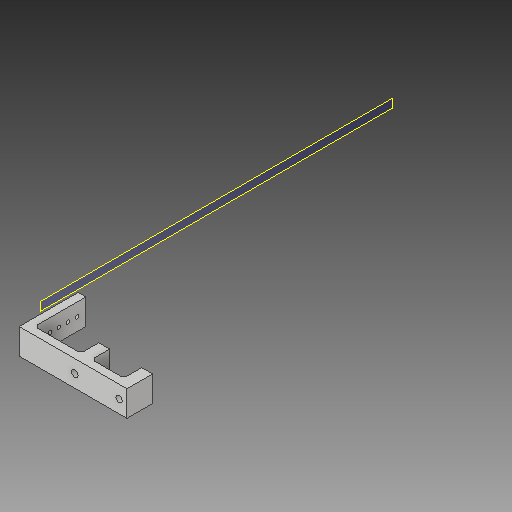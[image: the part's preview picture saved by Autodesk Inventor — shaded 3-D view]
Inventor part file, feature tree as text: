
AUTODESK INVENTOR PART (.ipt)
format: ipt  version: 2019.4 (Build 234330000, 330)  size: 150,528 bytes
history: native  units: mm
features: other x5, reference x4, extrude x3, sketch x3, plane x1, chamfer x1, projected_geometry x1
ambient origin geometry x8: Origin, YZ Plane, XZ Plane, XY Plane, X Axis, Y Axis, Z Axis, Center Point
bodies: Solid1 (feature_tree)
feature tree (18):
  plane  "Work Plane1"
  extrude  "Extrusion1"  Depth=20.0mm
  extrude  "Extrusion2"  Depth=5.0mm
  chamfer  "Chamfer1"  Distance=10.0mm
  extrude  "Extrusion3"  Depth=6.0mm TaperAngle=0.0deg
  sketch  "Sketch1"  dims[d0=40.0mm d1=20.0mm]
  reference  "Reference1"
  reference  "Reference2"
  sketch  "Sketch2"  dims[d2=2.8mm d3=5.0mm]
  projected_geometry  "Projected Loop1"
  sketch  "Sketch3"  dims[d4=10.0mm d5=60.0mm d7=7.0mm d8=10.0mm d10=10.0mm d12=6.0mm d13=0.0mm d14=84.0mm d15=6.0mm d16=8.5mm d17=36.0mm d18=8.5mm d19=10.0mm d20=0.0mm d21=2.0mm d22=2.0mm d23=45.0deg d24=10.0mm d25=0.0mm d26=4.9mm]
  reference  "Reference3"
  reference  "Reference4"
  other  "Assembly_neje_slide_y_wellplateholder_20mmrod.iam"
  other  "Assembly_neje_slide_y_20mmrod:1"
  other  "Neje_Base_Rod_20mm_250mm:1"
  other  "Neje_Rolls_small:1"
  other  "Neje_Rolls_small:2"
